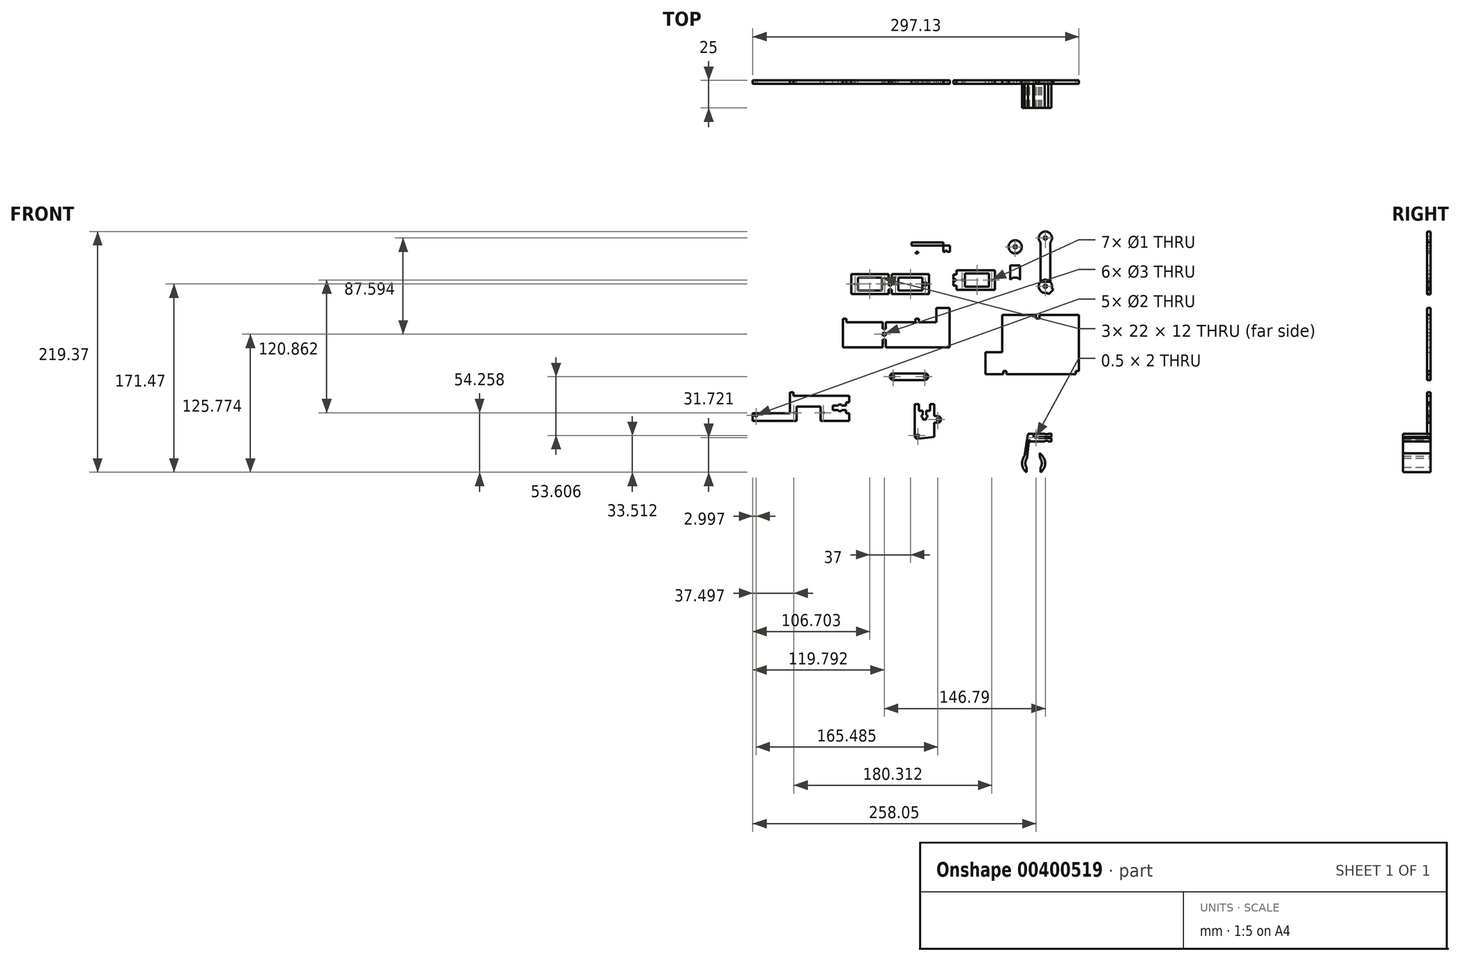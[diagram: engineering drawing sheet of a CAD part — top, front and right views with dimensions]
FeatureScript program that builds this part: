
annotation { "Feature Type Name" : "Feature", "Feature Type Description" : "" }
export const myFeature = defineFeature(function(context is Context, id is Id, definition is map)
    precondition{}
    {
        {
            var Q0;
            Q0=qCreatedBy(makeId("Front.planeOp"),FACE);
            var sketch = newSketch(context, id + "F0", { "sketchPlane" : qUnion([Q0])});
            skLineSegment(sketch, "E0", {"start": v(0, 0) * mm, "end": v(31, 0) * mm});
            skLineSegment(sketch, "E1", {"start": v(31, 0) * mm, "end": v(31, -3) * mm});
            skLineSegment(sketch, "E2", {"start": v(31, -3) * mm, "end": v(34, -3) * mm});
            skLineSegment(sketch, "E3", {"start": v(34, -3) * mm, "end": v(34, 0) * mm});
            skLineSegment(sketch, "E4", {"start": v(34, 0) * mm, "end": v(70, 0) * mm});
            skLineSegment(sketch, "E5", {"start": v(70, 0) * mm, "end": v(70, -51) * mm});
            skLineSegment(sketch, "E6", {"start": v(70, -51) * mm, "end": v(67, -51) * mm});
            skLineSegment(sketch, "E7", {"start": v(67, -51) * mm, "end": v(67, -54) * mm});
            skLineSegment(sketch, "E8", {"start": v(67, -54) * mm, "end": v(4, -54) * mm});
            skLineSegment(sketch, "E9", {"start": v(4, -54) * mm, "end": v(4, -51) * mm});
            skLineSegment(sketch, "E10", {"start": v(4, -51) * mm, "end": v(1, -51) * mm});
            skLineSegment(sketch, "E11", {"start": v(1, -51) * mm, "end": v(1, -54) * mm});
            skLineSegment(sketch, "E12", {"start": v(1, -54) * mm, "end": v(-15, -54) * mm});
            skLineSegment(sketch, "E13", {"start": v(-15, -54) * mm, "end": v(-15, -34) * mm});
            skLineSegment(sketch, "E14", {"start": v(-15, -34) * mm, "end": v(0, -34) * mm});
            skLineSegment(sketch, "E15", {"start": v(0, -34) * mm, "end": v(0, 0) * mm});
            skSolve(sketch);
        }
        {
            var Q0;
            Q0=makeQuery(id+"F0.imprint","IMPRINT",FACE,{"disambiguationData":[TD([[makeQuery(id+"F0.imprint","IMPRINT",EDGE,{"derivedFrom":sQuery(id+"F0.wireOp",EDGE,"E0")}),-1.0]])]});
            extrude(context, id + "F1", {"entities" : qUnion([Q0]), "depth" : 3 * mm});
        }
        {
            var Q0;
            Q0=qCreatedBy(makeId("Front.planeOp"),FACE);
            var sketch = newSketch(context, id + "F2", { "sketchPlane" : qUnion([Q0])});
            skLineSegment(sketch, "E16", {"start": v(-47.84, -29.56) * mm, "end": v(-105.84, -29.56) * mm});
            skLineSegment(sketch, "E17", {"start": v(-105.84, -29.56) * mm, "end": v(-105.84, -22.56) * mm});
            skLineSegment(sketch, "E18", {"start": v(-105.84, -22.56) * mm, "end": v(-108.84, -22.56) * mm});
            skLineSegment(sketch, "E19", {"start": v(-108.84, -22.56) * mm, "end": v(-108.84, -29.56) * mm});
            skPoint(sketch, "E20.endSnap0", {"position": v(-157.78, -10) * mm});
            skLineSegment(sketch, "E21", {"start": v(-108.84, -6.56) * mm, "end": v(-108.84, -12.56) * mm});
            skLineSegment(sketch, "E22", {"start": v(-108.84, -12.56) * mm, "end": v(-105.84, -12.56) * mm});
            skLineSegment(sketch, "E23", {"start": v(-105.84, -12.56) * mm, "end": v(-105.84, -6.56) * mm});
            skLineSegment(sketch, "E24", {"start": v(-105.84, -6.56) * mm, "end": v(-78.84, -6.56) * mm});
            skLineSegment(sketch, "E25", {"start": v(-78.84, -6.56) * mm, "end": v(-78.84, -3.56) * mm});
            skLineSegment(sketch, "E26", {"start": v(-78.84, -3.56) * mm, "end": v(-75.84, -3.56) * mm});
            skLineSegment(sketch, "E27", {"start": v(-75.84, -3.56) * mm, "end": v(-75.84, -6.56) * mm});
            skLineSegment(sketch, "E28", {"start": v(-75.84, -6.56) * mm, "end": v(-59.84, -6.56) * mm});
            skLineSegment(sketch, "E29", {"start": v(-59.84, -6.56) * mm, "end": v(-59.84, 6.44) * mm});
            skLineSegment(sketch, "E30", {"start": v(-59.84, 6.44) * mm, "end": v(-47.84, 6.44) * mm});
            skLineSegment(sketch, "E31", {"start": v(-108.84, -12.56) * mm, "end": v(-107.34, -12.56) * mm});
            skLineSegment(sketch, "E32", {"start": v(-59.84, 6.44) * mm, "end": v(-59.84, 4.44) * mm});
            skLineSegment(sketch, "E33", {"start": v(-58.78, 6.44) * mm, "end": v(-61.78, 6.44) * mm});
            skLineSegment(sketch, "E34.bottom", {"start": v(-62.78, 11) * mm, "end": v(-67.78, 11) * mm});
            skLineSegment(sketch, "E34.top", {"start": v(-62.78, 8) * mm, "end": v(-67.78, 8) * mm});
            skLineSegment(sketch, "E34.left", {"start": v(-62.78, 11) * mm, "end": v(-62.78, 8) * mm});
            skLineSegment(sketch, "E34.right", {"start": v(-67.78, 11) * mm, "end": v(-67.78, 8) * mm});
            skLineSegment(sketch, "E35", {"start": v(-47.84, 6.44) * mm, "end": v(-47.84, -29.56) * mm});
            skLineSegment(sketch, "E36", {"start": v(-108.84, -6.56) * mm, "end": v(-141.84, -6.56) * mm});
            skLineSegment(sketch, "E37", {"start": v(-141.84, -6.56) * mm, "end": v(-141.84, -3.56) * mm});
            skLineSegment(sketch, "E38", {"start": v(-141.84, -3.56) * mm, "end": v(-144.84, -3.56) * mm});
            skLineSegment(sketch, "E39", {"start": v(-144.84, -3.56) * mm, "end": v(-144.84, -6.56) * mm});
            skLineSegment(sketch, "E40", {"start": v(-144.84, -6.56) * mm, "end": v(-144.84, -29.56) * mm});
            skLineSegment(sketch, "E41", {"start": v(-144.84, -29.56) * mm, "end": v(-108.84, -29.56) * mm});
            skLineSegment(sketch, "E42", {"start": v(-108.84, -12.56) * mm, "end": v(-108.84, -17.56) * mm});
            skLineSegment(sketch, "E43", {"start": v(-108.84, -17.56) * mm, "end": v(-107.34, -17.56) * mm});
            skCircle(sketch, "E44", {"center": v(-107.34, -17.56) * mm, "radius": 1.5 * mm});
            skSolve(sketch);
        }
        {
            var Q0;
            Q0=makeQuery(id+"F2.imprint","IMPRINT",FACE,{"disambiguationData":[TD([[makeQuery(id+"F2.imprint","IMPRINT",EDGE,{"derivedFrom":sQuery(id+"F2.wireOp",EDGE,"E16")}),-1.0]])]});
            extrude(context, id + "F3", {"entities" : qUnion([Q0]), "depth" : 3 * mm});
        }
        {
            var Q0;
            Q0=qCreatedBy(makeId("Front.planeOp"),FACE);
            var sketch = newSketch(context, id + "F4", { "sketchPlane" : qUnion([Q0])});
            skLineSegment(sketch, "E45", {"start": v(-66.43, 19.14) * mm, "end": v(-66.43, 37.14) * mm});
            skLineSegment(sketch, "E46", {"start": v(-66.43, 37.14) * mm, "end": v(-100.43, 37.14) * mm});
            skLineSegment(sketch, "E47", {"start": v(-66.43, 19.14) * mm, "end": v(-100.43, 19.14) * mm});
            skLineSegment(sketch, "E48", {"start": v(-100.43, 19.14) * mm, "end": v(-100.43, 23.14) * mm});
            skLineSegment(sketch, "E49", {"start": v(-100.43, 23.14) * mm, "end": v(-103.43, 23.14) * mm});
            skLineSegment(sketch, "E50", {"start": v(-103.43, 23.14) * mm, "end": v(-103.43, 19.14) * mm});
            skLineSegment(sketch, "E51", {"start": v(-100.43, 37.14) * mm, "end": v(-100.43, 33.14) * mm});
            skLineSegment(sketch, "E52", {"start": v(-100.43, 33.14) * mm, "end": v(-103.43, 33.14) * mm});
            skLineSegment(sketch, "E53", {"start": v(-103.43, 33.14) * mm, "end": v(-103.43, 37.14) * mm});
            skLineSegment(sketch, "E54", {"start": v(-103.43, 37.14) * mm, "end": v(-137.43, 37.14) * mm});
            skLineSegment(sketch, "E55", {"start": v(-137.43, 37.14) * mm, "end": v(-137.43, 19.14) * mm});
            skLineSegment(sketch, "E56", {"start": v(-137.43, 19.14) * mm, "end": v(-103.43, 19.14) * mm});
            skLineSegment(sketch, "E57", {"start": v(-137.43, 37.14) * mm, "end": v(-131.43, 37.14) * mm});
            skLineSegment(sketch, "E58.bottom", {"start": v(-131.43, 22.14) * mm, "end": v(-109.43, 22.14) * mm});
            skLineSegment(sketch, "E58.top", {"start": v(-131.43, 34.14) * mm, "end": v(-109.43, 34.14) * mm});
            skLineSegment(sketch, "E58.left", {"start": v(-131.43, 22.14) * mm, "end": v(-131.43, 34.14) * mm});
            skLineSegment(sketch, "E58.right", {"start": v(-109.43, 22.14) * mm, "end": v(-109.43, 34.14) * mm});
            skLineSegment(sketch, "E59", {"start": v(-66.43, 37.14) * mm, "end": v(-72.43, 37.14) * mm});
            skLineSegment(sketch, "E60.bottom", {"start": v(-72.43, 34.14) * mm, "end": v(-94.43, 34.14) * mm});
            skLineSegment(sketch, "E60.top", {"start": v(-72.43, 22.14) * mm, "end": v(-94.43, 22.14) * mm});
            skLineSegment(sketch, "E60.left", {"start": v(-72.43, 34.14) * mm, "end": v(-72.43, 22.14) * mm});
            skLineSegment(sketch, "E60.right", {"start": v(-94.43, 34.14) * mm, "end": v(-94.43, 22.14) * mm});
            skCircle(sketch, "E61", {"center": v(-101.93, 28.14) * mm, "radius": 1.5 * mm});
            skLineSegment(sketch, "E62", {"start": v(-66.43, 37.14) * mm, "end": v(-69.93, 37.14) * mm});
            skCircle(sketch, "E63", {"center": v(-69.93, 28.14) * mm, "radius": 1.5 * mm});
            skLineSegment(sketch, "E64", {"start": v(-131.43, 37.14) * mm, "end": v(-133.93, 37.14) * mm});
            skCircle(sketch, "E65", {"center": v(-133.93, 28.14) * mm, "radius": 0.5 * mm});
            skCircle(sketch, "E66", {"center": v(-106.93, 28.14) * mm, "radius": 0.5 * mm});
            skCircle(sketch, "E67", {"center": v(-96.93, 28.14) * mm, "radius": 0.5 * mm});
            skSolve(sketch);
        }
        {
            var Q0;
            Q0=makeQuery(id+"F4.imprint","IMPRINT",FACE,{"disambiguationData":[TD([[makeQuery(id+"F4.imprint","IMPRINT",EDGE,{"derivedFrom":sQuery(id+"F4.wireOp",EDGE,"E45")}),1.0]])]});
            extrude(context, id + "F5", {"entities" : qUnion([Q0]), "depth" : 3 * mm});
        }
        {
            var Q0;
            Q0=qCreatedBy(makeId("Front.planeOp"),FACE);
            var sketch = newSketch(context, id + "F6", { "sketchPlane" : qUnion([Q0])});
            skLineSegment(sketch, "E68", {"start": v(-6.38, 22.79) * mm, "end": v(-41.38, 22.79) * mm});
            skLineSegment(sketch, "E69", {"start": v(-6.38, 22.79) * mm, "end": v(-6.38, 40.79) * mm});
            skLineSegment(sketch, "E70", {"start": v(-6.38, 40.79) * mm, "end": v(-41.38, 40.79) * mm});
            skLineSegment(sketch, "E71", {"start": v(-41.38, 40.79) * mm, "end": v(-41.38, 36.79) * mm});
            skLineSegment(sketch, "E72", {"start": v(-41.38, 36.79) * mm, "end": v(-44.38, 36.79) * mm});
            skLineSegment(sketch, "E73", {"start": v(-44.38, 36.79) * mm, "end": v(-44.38, 26.79) * mm});
            skLineSegment(sketch, "E74", {"start": v(-44.38, 26.79) * mm, "end": v(-41.38, 26.79) * mm});
            skLineSegment(sketch, "E75", {"start": v(-41.38, 26.79) * mm, "end": v(-41.38, 22.79) * mm});
            skLineSegment(sketch, "E76", {"start": v(-6.38, 40.79) * mm, "end": v(-12.38, 40.79) * mm});
            skLineSegment(sketch, "E77.bottom", {"start": v(-11.82, 37.79) * mm, "end": v(-33.82, 37.79) * mm});
            skLineSegment(sketch, "E77.top", {"start": v(-11.82, 25.79) * mm, "end": v(-33.82, 25.79) * mm});
            skLineSegment(sketch, "E77.left", {"start": v(-11.82, 37.79) * mm, "end": v(-11.82, 25.79) * mm});
            skLineSegment(sketch, "E77.right", {"start": v(-33.82, 37.79) * mm, "end": v(-33.82, 25.79) * mm});
            skLineSegment(sketch, "E78", {"start": v(-12.38, 40.79) * mm, "end": v(-7.38, 40.79) * mm});
            skLineSegment(sketch, "E79", {"start": v(-12.38, 40.79) * mm, "end": v(-9.38, 40.79) * mm});
            skLineSegment(sketch, "E80", {"start": v(-12.38, 40.79) * mm, "end": v(-9.88, 40.79) * mm});
            skLineSegment(sketch, "E81", {"start": v(-33.82, 40.79) * mm, "end": v(-36.32, 40.79) * mm});
            skLineSegment(sketch, "E82", {"start": v(-44.38, 36.79) * mm, "end": v(-44.38, 32.25) * mm});
            skLineSegment(sketch, "E83", {"start": v(-41.38, 36.79) * mm, "end": v(-41.38, 31.79) * mm});
            skLineSegment(sketch, "E84", {"start": v(-41.38, 31.79) * mm, "end": v(-6.38, 31.79) * mm});
            skLineSegment(sketch, "E85", {"start": v(-33.82, 31.79) * mm, "end": v(-34.96, 31.79) * mm});
            skSolve(sketch);
        }
        {
            var Q0;
            {var subQ12=sQuery(id+"F6.wireOp",EDGE,"E71");Q0=makeQuery(id+"F6.imprint","IMPRINT",FACE,{"disambiguationData":[TD([[makeQuery(id+"F6.imprint","IMPRINT",EDGE,{"derivedFrom":subQ12}),1.0]])]});}
            var Q1;
            {var subQ6=sQuery(id+"F6.wireOp",EDGE,"E68");Q1=makeQuery(id+"F6.imprint","IMPRINT",FACE,{"disambiguationData":[TD([[makeQuery(id+"F6.imprint","IMPRINT",EDGE,{"derivedFrom":subQ6}),-1.0]])]});}
            extrude(context, id + "F7", {"entities" : qUnion([Q0, Q1]), "depth" : 3 * mm});
        }
        {
            var Q0;
            Q0=makeQuery(id+"F7.opExtrude","CAP_FACE",FACE,{"disambiguationData":[OSD([sQuery(id+"F6.wireOp",EDGE,"E68"),sQuery(id+"F6.wireOp",EDGE,"E69"),sQuery(id+"F6.wireOp",EDGE,"E70"),sQuery(id+"F6.wireOp",EDGE,"E71"),sQuery(id+"F6.wireOp",EDGE,"E72"),sQuery(id+"F6.wireOp",EDGE,"E73"),sQuery(id+"F6.wireOp",EDGE,"E74"),sQuery(id+"F6.wireOp",EDGE,"E75"),sQuery(id+"F6.wireOp",EDGE,"E76"),sQuery(id+"F6.wireOp",EDGE,"E77.bottom"),sQuery(id+"F6.wireOp",EDGE,"E77.top"),sQuery(id+"F6.wireOp",EDGE,"E77.left"),sQuery(id+"F6.wireOp",EDGE,"E77.right"),sQuery(id+"F6.wireOp",EDGE,"E78"),sQuery(id+"F6.wireOp",EDGE,"E79"),sQuery(id+"F6.wireOp",EDGE,"E80"),sQuery(id+"F6.wireOp",EDGE,"E81"),sQuery(id+"F6.wireOp",EDGE,"E82")])],"isStart":false});
            var sketch = newSketch(context, id + "F8", { "sketchPlane" : qUnion([Q0])});
            skCircle(sketch, "E86", {"center": v(-36.32, 31.79) * mm, "radius": 0.5 * mm});
            skLineSegment(sketch, "E87", {"start": v(-9.32, 31.79) * mm, "end": v(-9.7, 31.79) * mm});
            skCircle(sketch, "E88", {"center": v(-9.32, 31.79) * mm, "radius": 0.5 * mm});
            skLineSegment(sketch, "E89", {"start": v(-44.38, 36.79) * mm, "end": v(-44.38, 31.79) * mm});
            skLineSegment(sketch, "E90", {"start": v(-44.38, 31.79) * mm, "end": v(-43.38, 31.79) * mm});
            skCircle(sketch, "E91", {"center": v(-43.38, 31.79) * mm, "radius": 1 * mm});
            skSolve(sketch);
        }
        {
            var Q0;
            Q0=makeQuery(id+"F8.imprint","IMPRINT",FACE,{"disambiguationData":[TD([[makeQuery(id+"F8.imprint","IMPRINT",EDGE,{"derivedFrom":sQuery(id+"F8.wireOp",EDGE,"E86")}),1.0]])]});
            var Q1;
            Q1=makeQuery(id+"F8.imprint","IMPRINT",FACE,{"disambiguationData":[TD([[makeQuery(id+"F8.imprint","IMPRINT",EDGE,{"derivedFrom":sQuery(id+"F8.wireOp",EDGE,"E88")}),1.0]])]});
            extrude(context, id + "F9", {"entities" : qUnion([Q0, Q1]), "operationType" : NewBodyOperationType.REMOVE, "oppositeDirection" : true, "depth" : 25 * mm});
        }
        {
            var Q0;
            Q0=makeQuery(id+"F8.imprint","IMPRINT",FACE,{"disambiguationData":[TD([[makeQuery(id+"F8.imprint","IMPRINT",EDGE,{"derivedFrom":sQuery(id+"F8.wireOp",EDGE,"E86")}),-1.0]])]});
            var sketch = newSketch(context, id + "F10", { "sketchPlane" : qUnion([Q0])});
            skCircle(sketch, "E92", {"center": v(-43.41, 31.78) * mm, "radius": 1 * mm});
            skSolve(sketch);
        }
        {
            var Q0;
            Q0 = qSketchRegion(id + "F10", true);
            extrude(context, id + "F11", {"entities" : qUnion([Q0]), "operationType" : NewBodyOperationType.REMOVE, "oppositeDirection" : true, "depth" : 25 * mm});
        }
        {
            var Q0;
            Q0=qCreatedBy(makeId("Front.planeOp"),FACE);
            var sketch = newSketch(context, id + "F12", { "sketchPlane" : qUnion([Q0])});
            skLineSegment(sketch, "E93", {"start": v(-227.13, -96.57) * mm, "end": v(-187.13, -96.57) * mm});
            skLineSegment(sketch, "E94", {"start": v(-187.13, -96.57) * mm, "end": v(-187.13, -83.57) * mm});
            skLineSegment(sketch, "E95", {"start": v(-187.13, -83.57) * mm, "end": v(-165.13, -83.57) * mm});
            skLineSegment(sketch, "E96", {"start": v(-165.13, -83.57) * mm, "end": v(-165.13, -96.57) * mm});
            skLineSegment(sketch, "E97", {"start": v(-165.13, -96.57) * mm, "end": v(-139.13, -96.57) * mm});
            skLineSegment(sketch, "E98", {"start": v(-227.13, -96.57) * mm, "end": v(-227.13, -89.57) * mm});
            skLineSegment(sketch, "E99", {"start": v(-227.13, -89.57) * mm, "end": v(-193.13, -89.57) * mm});
            skLineSegment(sketch, "E100", {"start": v(-193.13, -89.57) * mm, "end": v(-193.13, -70.57) * mm});
            skLineSegment(sketch, "E101", {"start": v(-193.13, -70.57) * mm, "end": v(-190.13, -70.57) * mm});
            skLineSegment(sketch, "E102", {"start": v(-139.13, -96.57) * mm, "end": v(-139.13, -89.57) * mm});
            skLineSegment(sketch, "E103", {"start": v(-139.13, -89.57) * mm, "end": v(-142.13, -89.57) * mm});
            skLineSegment(sketch, "E104", {"start": v(-190.13, -70.57) * mm, "end": v(-190.13, -73.57) * mm});
            skLineSegment(sketch, "E105", {"start": v(-190.13, -73.57) * mm, "end": v(-139.13, -73.57) * mm});
            skLineSegment(sketch, "E106", {"start": v(-139.13, -73.57) * mm, "end": v(-139.13, -79.57) * mm});
            skLineSegment(sketch, "E107", {"start": v(-139.13, -79.57) * mm, "end": v(-142.13, -79.57) * mm});
            skLineSegment(sketch, "E108", {"start": v(-142.13, -79.57) * mm, "end": v(-142.13, -82.57) * mm});
            skLineSegment(sketch, "E109", {"start": v(-142.13, -82.57) * mm, "end": v(-146.13, -82.57) * mm});
            skLineSegment(sketch, "E110", {"start": v(-142.13, -89.57) * mm, "end": v(-142.13, -86.57) * mm});
            skLineSegment(sketch, "E111", {"start": v(-142.13, -86.57) * mm, "end": v(-146.13, -86.57) * mm});
            skLineSegment(sketch, "E112", {"start": v(-146.13, -82.57) * mm, "end": v(-146.13, -81.57) * mm});
            skLineSegment(sketch, "E113", {"start": v(-146.13, -81.57) * mm, "end": v(-149.13, -81.57) * mm});
            skLineSegment(sketch, "E114", {"start": v(-149.13, -81.57) * mm, "end": v(-149.13, -82.57) * mm});
            skLineSegment(sketch, "E115", {"start": v(-149.13, -82.57) * mm, "end": v(-154.13, -82.57) * mm});
            skLineSegment(sketch, "E116", {"start": v(-154.13, -82.57) * mm, "end": v(-154.13, -86.57) * mm});
            skLineSegment(sketch, "E117", {"start": v(-154.13, -86.57) * mm, "end": v(-149.13, -86.57) * mm});
            skLineSegment(sketch, "E118", {"start": v(-149.13, -86.57) * mm, "end": v(-149.13, -87.57) * mm});
            skLineSegment(sketch, "E119", {"start": v(-149.13, -87.57) * mm, "end": v(-146.13, -87.57) * mm});
            skLineSegment(sketch, "E120", {"start": v(-146.13, -87.57) * mm, "end": v(-146.13, -86.57) * mm});
            skSolve(sketch);
        }
        {
            var Q0;
            Q0=makeQuery(id+"F12.imprint","IMPRINT",FACE,{"disambiguationData":[TD([[makeQuery(id+"F12.imprint","IMPRINT",EDGE,{"derivedFrom":sQuery(id+"F12.wireOp",EDGE,"E93")}),1.0]])]});
            extrude(context, id + "F13", {"entities" : qUnion([Q0]), "depth" : 3 * mm});
        }
        {
            var Q0;
            Q0=makeQuery(id+"F13.opExtrude","CAP_FACE",FACE,{"disambiguationData":[OSD([sQuery(id+"F12.wireOp",EDGE,"E93"),sQuery(id+"F12.wireOp",EDGE,"E94"),sQuery(id+"F12.wireOp",EDGE,"E95"),sQuery(id+"F12.wireOp",EDGE,"E96"),sQuery(id+"F12.wireOp",EDGE,"E97"),sQuery(id+"F12.wireOp",EDGE,"E98"),sQuery(id+"F12.wireOp",EDGE,"E99"),sQuery(id+"F12.wireOp",EDGE,"E100"),sQuery(id+"F12.wireOp",EDGE,"E101"),sQuery(id+"F12.wireOp",EDGE,"E102"),sQuery(id+"F12.wireOp",EDGE,"E103"),sQuery(id+"F12.wireOp",EDGE,"E104"),sQuery(id+"F12.wireOp",EDGE,"E105"),sQuery(id+"F12.wireOp",EDGE,"E106"),sQuery(id+"F12.wireOp",EDGE,"E107"),sQuery(id+"F12.wireOp",EDGE,"E108"),sQuery(id+"F12.wireOp",EDGE,"E109"),sQuery(id+"F12.wireOp",EDGE,"E110"),sQuery(id+"F12.wireOp",EDGE,"E111"),sQuery(id+"F12.wireOp",EDGE,"E112"),sQuery(id+"F12.wireOp",EDGE,"E113"),sQuery(id+"F12.wireOp",EDGE,"E114"),sQuery(id+"F12.wireOp",EDGE,"E115"),sQuery(id+"F12.wireOp",EDGE,"E116"),sQuery(id+"F12.wireOp",EDGE,"E117"),sQuery(id+"F12.wireOp",EDGE,"E118"),sQuery(id+"F12.wireOp",EDGE,"E119"),sQuery(id+"F12.wireOp",EDGE,"E120")])],"isStart":false});
            var sketch = newSketch(context, id + "F14", { "sketchPlane" : qUnion([Q0])});
            skCircle(sketch, "E121", {"center": v(-224.13, -91.57) * mm, "radius": 1 * mm});
            skCircle(sketch, "E122", {"center": v(-189.63, -89.07) * mm, "radius": 0.5 * mm});
            skCircle(sketch, "E123", {"center": v(-162.63, -89.07) * mm, "radius": 0.5 * mm});
            skSolve(sketch);
        }
        {
            var Q0;
            Q0=makeQuery(id+"F14.imprint","IMPRINT",FACE,{"disambiguationData":[TD([[makeQuery(id+"F14.imprint","IMPRINT",EDGE,{"derivedFrom":sQuery(id+"F14.wireOp",EDGE,"E121")}),1.0]])]});
            var Q1;
            Q1=makeQuery(id+"F14.imprint","IMPRINT",FACE,{"disambiguationData":[TD([[makeQuery(id+"F14.imprint","IMPRINT",EDGE,{"derivedFrom":sQuery(id+"F14.wireOp",EDGE,"E122")}),1.0]])]});
            var Q2;
            Q2=makeQuery(id+"F14.imprint","IMPRINT",FACE,{"disambiguationData":[TD([[makeQuery(id+"F14.imprint","IMPRINT",EDGE,{"derivedFrom":sQuery(id+"F14.wireOp",EDGE,"E123")}),1.0]])]});
            extrude(context, id + "F15", {"entities" : qUnion([Q0, Q1, Q2]), "operationType" : NewBodyOperationType.REMOVE, "oppositeDirection" : true, "depth" : 25 * mm});
        }
        {
            var Q0;
            Q0=qCreatedBy(makeId("Front.planeOp"),FACE);
            var sketch = newSketch(context, id + "F16", { "sketchPlane" : qUnion([Q0])});
            skLineSegment(sketch, "E124.bottom", {"start": v(-99.2, -53.21) * mm, "end": v(-70.2, -53.21) * mm});
            skLineSegment(sketch, "E124.top", {"start": v(-99.2, -59.21) * mm, "end": v(-70.2, -59.21) * mm});
            skLineSegment(sketch, "E124.left", {"start": v(-102.2, -56.21) * mm, "end": v(-102.2, -56.21) * mm});
            skLineSegment(sketch, "E124.right", {"start": v(-67.2, -56.21) * mm, "end": v(-67.2, -56.21) * mm});
            skPoint(sketch, "E125.visualSharp", {"position": v(-102.2, -53.21) * mm});
            skArc(sketch, "E125.filletArc", {"start": v(-99.2, -53.21) * mm, "mid": v(-101.33, -54.1) * mm, "end": v(-102.2, -56.21) * mm});
            skPoint(sketch, "E126.visualSharp", {"position": v(-102.2, -59.21) * mm});
            skArc(sketch, "E126.filletArc", {"start": v(-102.2, -56.21) * mm, "mid": v(-101.33, -58.33) * mm, "end": v(-99.2, -59.21) * mm});
            skPoint(sketch, "E127.visualSharp", {"position": v(-67.2, -53.21) * mm});
            skArc(sketch, "E127.filletArc", {"start": v(-67.2, -56.21) * mm, "mid": v(-68.09, -54.1) * mm, "end": v(-70.2, -53.21) * mm});
            skPoint(sketch, "E128.visualSharp", {"position": v(-67.2, -59.21) * mm});
            skArc(sketch, "E128.filletArc", {"start": v(-70.2, -59.21) * mm, "mid": v(-68.09, -58.33) * mm, "end": v(-67.2, -56.21) * mm});
            skLineSegment(sketch, "E129", {"start": v(-102.2, -56.21) * mm, "end": v(-66.67, -56.21) * mm});
            skLineSegment(sketch, "E130", {"start": v(-102.2, -56.21) * mm, "end": v(-99.2, -56.21) * mm});
            skLineSegment(sketch, "E131", {"start": v(-99.2, -56.21) * mm, "end": v(-70.2, -56.21) * mm});
            skCircle(sketch, "E132", {"center": v(-99.2, -56.21) * mm, "radius": 1 * mm});
            skCircle(sketch, "E133", {"center": v(-70.2, -56.21) * mm, "radius": 1 * mm});
            skSolve(sketch);
        }
        {
            var Q0;
            Q0=makeQuery(id+"F16.imprint","IMPRINT",FACE,{"disambiguationData":[TD([[makeQuery(id+"F16.imprint","IMPRINT",EDGE,{"derivedFrom":sQuery(id+"F16.wireOp",EDGE,"E124.top")}),1.0]])]});
            var Q1;
            Q1=makeQuery(id+"F16.imprint","IMPRINT",FACE,{"disambiguationData":[TD([[makeQuery(id+"F16.imprint","IMPRINT",EDGE,{"derivedFrom":sQuery(id+"F16.wireOp",EDGE,"E124.bottom")}),-1.0]])]});
            extrude(context, id + "F17", {"entities" : qUnion([Q0, Q1]), "depth" : 3 * mm});
        }
        {
            var Q0;
            Q0=qCreatedBy(makeId("Front.planeOp"),FACE);
            var sketch = newSketch(context, id + "F18", { "sketchPlane" : qUnion([Q0])});
            skLineSegment(sketch, "E134", {"start": v(-75.65, -87.17) * mm, "end": v(-72.15, -87.17) * mm});
            skLineSegment(sketch, "E135", {"start": v(-72.15, -87.17) * mm, "end": v(-72.15, -91.17) * mm});
            skLineSegment(sketch, "E136", {"start": v(-72.15, -91.17) * mm, "end": v(-73.15, -91.17) * mm});
            skLineSegment(sketch, "E137", {"start": v(-73.15, -91.17) * mm, "end": v(-73.15, -93.17) * mm});
            skLineSegment(sketch, "E138", {"start": v(-73.15, -93.17) * mm, "end": v(-72.15, -93.17) * mm});
            skLineSegment(sketch, "E139", {"start": v(-72.15, -93.17) * mm, "end": v(-72.15, -95.17) * mm});
            skLineSegment(sketch, "E140", {"start": v(-72.15, -95.17) * mm, "end": v(-69.15, -95.17) * mm});
            skLineSegment(sketch, "E141", {"start": v(-69.15, -95.17) * mm, "end": v(-69.15, -93.17) * mm});
            skLineSegment(sketch, "E142", {"start": v(-69.15, -93.17) * mm, "end": v(-68.15, -93.17) * mm});
            skLineSegment(sketch, "E143", {"start": v(-68.15, -93.17) * mm, "end": v(-68.15, -91.17) * mm});
            skLineSegment(sketch, "E144", {"start": v(-68.15, -91.17) * mm, "end": v(-69.15, -91.17) * mm});
            skLineSegment(sketch, "E145", {"start": v(-69.15, -91.17) * mm, "end": v(-69.15, -87.17) * mm});
            skLineSegment(sketch, "E146", {"start": v(-65.65, -87.17) * mm, "end": v(-65.65, -81.17) * mm});
            skLineSegment(sketch, "E147", {"start": v(-65.65, -81.17) * mm, "end": v(-61.65, -81.17) * mm});
            skLineSegment(sketch, "E148", {"start": v(-61.65, -81.17) * mm, "end": v(-61.65, -92.17) * mm});
            skLineSegment(sketch, "E149", {"start": v(-61.65, -92.17) * mm, "end": v(-58.65, -92.17) * mm});
            skLineSegment(sketch, "E150", {"start": v(-55.65, -95.17) * mm, "end": v(-55.65, -95.17) * mm});
            skLineSegment(sketch, "E151", {"start": v(-58.65, -98.17) * mm, "end": v(-61.65, -98.17) * mm});
            skLineSegment(sketch, "E152", {"start": v(-61.65, -98.17) * mm, "end": v(-61.65, -111.17) * mm});
            skPoint(sketch, "E153.visualSharp", {"position": v(-55.65, -98.17) * mm});
            skArc(sketch, "E153.filletArc", {"start": v(-58.65, -98.17) * mm, "mid": v(-56.53, -97.3) * mm, "end": v(-55.65, -95.17) * mm});
            skPoint(sketch, "E154.visualSharp", {"position": v(-55.65, -92.17) * mm});
            skArc(sketch, "E154.filletArc", {"start": v(-55.65, -95.17) * mm, "mid": v(-56.53, -93.05) * mm, "end": v(-58.65, -92.17) * mm});
            skLineSegment(sketch, "E155", {"start": v(-55.65, -95.17) * mm, "end": v(-57.65, -95.17) * mm});
            skLineSegment(sketch, "E156", {"start": v(-57.65, -95.17) * mm, "end": v(-58.65, -95.17) * mm});
            skCircle(sketch, "E157", {"center": v(-58.65, -95.17) * mm, "radius": 1 * mm});
            skLineSegment(sketch, "E158", {"start": v(-69.15, -87.17) * mm, "end": v(-65.65, -87.17) * mm});
            skLineSegment(sketch, "E159", {"start": v(-75.65, -87.17) * mm, "end": v(-75.65, -81.17) * mm});
            skLineSegment(sketch, "E160", {"start": v(-75.65, -81.17) * mm, "end": v(-79.65, -81.17) * mm});
            skLineSegment(sketch, "E161", {"start": v(-79.65, -81.17) * mm, "end": v(-79.65, -109.82) * mm});
            skLineSegment(sketch, "E162", {"start": v(-76.32, -112.8) * mm, "end": v(-61.65, -111.17) * mm});
            skPoint(sketch, "E163.visualSharp", {"position": v(-79.65, -113.17) * mm});
            skArc(sketch, "E163.filletArc", {"start": v(-79.65, -109.82) * mm, "mid": v(-78.65, -112.05) * mm, "end": v(-76.32, -112.8) * mm});
            skCircle(sketch, "E164", {"center": v(-76.65, -109.82) * mm, "radius": 1 * mm});
            skSolve(sketch);
        }
        {
            var Q0;
            Q0=makeQuery(id+"F18.imprint","IMPRINT",FACE,{"disambiguationData":[TD([[makeQuery(id+"F18.imprint","IMPRINT",EDGE,{"derivedFrom":sQuery(id+"F18.wireOp",EDGE,"E134")}),-1.0]])]});
            extrude(context, id + "F19", {"entities" : qUnion([Q0]), "depth" : 3 * mm});
        }
        {
            var Q0;
            Q0=qCreatedBy(makeId("Front.planeOp"),FACE);
            var sketch = newSketch(context, id + "F20", { "sketchPlane" : qUnion([Q0])});
            skLineSegment(sketch, "E165", {"start": v(11.96, 45.07) * mm, "end": v(16.46, 45.07) * mm});
            skLineSegment(sketch, "E166", {"start": v(16.46, 45.07) * mm, "end": v(7.46, 45.07) * mm});
            skLineSegment(sketch, "E167", {"start": v(16.46, 45.07) * mm, "end": v(16.46, 58.57) * mm});
            skLineSegment(sketch, "E168", {"start": v(16.46, 58.57) * mm, "end": v(16.46, 31.57) * mm});
            skLineSegment(sketch, "E169", {"start": v(7.46, 45.07) * mm, "end": v(7.46, 58.57) * mm});
            skLineSegment(sketch, "E170", {"start": v(7.46, 58.57) * mm, "end": v(7.46, 31.57) * mm});
            skLineSegment(sketch, "E171", {"start": v(11.96, 45.07) * mm, "end": v(11.96, 22.07) * mm});
            skLineSegment(sketch, "E172", {"start": v(11.96, 22.07) * mm, "end": v(11.96, 45.07) * mm});
            skLineSegment(sketch, "E173", {"start": v(11.96, 45.07) * mm, "end": v(11.96, 68.07) * mm});
            skLineSegment(sketch, "E174", {"start": v(11.96, 22.07) * mm, "end": v(11.96, 28.07) * mm});
            skCircle(sketch, "E175", {"center": v(11.96, 28.07) * mm, "radius": 6 * mm});
            skLineSegment(sketch, "E176", {"start": v(11.96, 68.07) * mm, "end": v(11.96, 62.07) * mm});
            skCircle(sketch, "E177", {"center": v(11.96, 62.07) * mm, "radius": 6 * mm});
            skCircle(sketch, "E178", {"center": v(11.96, 62.07) * mm, "radius": 1.5 * mm});
            skCircle(sketch, "E179", {"center": v(11.96, 28.07) * mm, "radius": 1.5 * mm});
            skSolve(sketch);
        }
        {
            var Q0;
            {var subQ0=sQuery(id+"F20.wireOp",EDGE,"E170");var subQ1=sQuery(id+"F20.wireOp",EDGE,"E166");var subQ2=makeQuery(id+"F20.imprint","INTERSECT",VERTEX,{"derivedFrom":[subQ1,subQ0]});Q0=makeQuery(id+"F20.imprint","IMPRINT",FACE,{"disambiguationData":[TD([[makeQuery(id+"F20.imprint","IMPRINT",EDGE,{"disambiguationData":[TD([[subQ2,-1.0]])],"derivedFrom":subQ0}),1.0]])]});}
            var Q1;
            {var subQ0=sQuery(id+"F20.wireOp",EDGE,"E168");var subQ1=sQuery(id+"F20.wireOp",EDGE,"E166");var subQ2=makeQuery(id+"F20.imprint","INTERSECT",VERTEX,{"derivedFrom":[subQ1,subQ0]});Q1=makeQuery(id+"F20.imprint","IMPRINT",FACE,{"disambiguationData":[TD([[makeQuery(id+"F20.imprint","IMPRINT",EDGE,{"disambiguationData":[TD([[subQ2,-1.0]])],"derivedFrom":subQ0}),-1.0]])]});}
            var Q2;
            {var subQ4=sQuery(id+"F20.wireOp",EDGE,"E172");var subQ6=sQuery(id+"F20.wireOp",EDGE,"E179");var subQ7=makeQuery(id+"F20.imprint","INTERSECT",VERTEX,{"derivedFrom":[subQ4,subQ6]});Q2=makeQuery(id+"F20.imprint","IMPRINT",FACE,{"disambiguationData":[TD([[makeQuery(id+"F20.imprint","IMPRINT",EDGE,{"disambiguationData":[TD([[subQ7,-1.0]])],"derivedFrom":subQ4}),1.0]])]});}
            var Q3;
            {var subQ2=sQuery(id+"F20.wireOp",EDGE,"E172");var subQ6=sQuery(id+"F20.wireOp",EDGE,"E179");var subQ8=makeQuery(id+"F20.imprint","INTERSECT",VERTEX,{"derivedFrom":[subQ2,subQ6]});Q3=makeQuery(id+"F20.imprint","IMPRINT",FACE,{"disambiguationData":[TD([[makeQuery(id+"F20.imprint","IMPRINT",EDGE,{"disambiguationData":[TD([[subQ8,-1.0]])],"derivedFrom":subQ2}),-1.0]])]});}
            var Q4;
            {var subQ0=sQuery(id+"F20.wireOp",EDGE,"E170");var subQ1=sQuery(id+"F20.wireOp",EDGE,"E166");var subQ2=makeQuery(id+"F20.imprint","INTERSECT",VERTEX,{"derivedFrom":[subQ1,subQ0]});Q4=makeQuery(id+"F20.imprint","IMPRINT",FACE,{"disambiguationData":[TD([[makeQuery(id+"F20.imprint","IMPRINT",EDGE,{"disambiguationData":[TD([[subQ2,1.0]])],"derivedFrom":subQ0}),1.0]])]});}
            var Q5;
            {var subQ0=sQuery(id+"F20.wireOp",EDGE,"E168");var subQ1=sQuery(id+"F20.wireOp",EDGE,"E166");var subQ2=makeQuery(id+"F20.imprint","INTERSECT",VERTEX,{"derivedFrom":[subQ1,subQ0]});Q5=makeQuery(id+"F20.imprint","IMPRINT",FACE,{"disambiguationData":[TD([[makeQuery(id+"F20.imprint","IMPRINT",EDGE,{"disambiguationData":[TD([[subQ2,1.0]])],"derivedFrom":subQ0}),-1.0]])]});}
            var Q6;
            {var subQ0=sQuery(id+"F20.wireOp",EDGE,"E177");var subQ2=sQuery(id+"F20.wireOp",EDGE,"E173");var subQ3=makeQuery(id+"F20.imprint","INTERSECT",VERTEX,{"derivedFrom":[subQ2,subQ0]});Q6=makeQuery(id+"F20.imprint","IMPRINT",FACE,{"disambiguationData":[TD([[makeQuery(id+"F20.imprint","IMPRINT",EDGE,{"disambiguationData":[TD([[subQ3,-1.0]])],"derivedFrom":subQ2}),1.0]])]});}
            var Q7;
            {var subQ0=sQuery(id+"F20.wireOp",EDGE,"E177");var subQ2=sQuery(id+"F20.wireOp",EDGE,"E173");var subQ3=makeQuery(id+"F20.imprint","INTERSECT",VERTEX,{"derivedFrom":[subQ2,subQ0]});Q7=makeQuery(id+"F20.imprint","IMPRINT",FACE,{"disambiguationData":[TD([[makeQuery(id+"F20.imprint","IMPRINT",EDGE,{"disambiguationData":[TD([[subQ3,-1.0]])],"derivedFrom":subQ2}),-1.0]])]});}
            extrude(context, id + "F21", {"entities" : qUnion([Q0, Q1, Q2, Q3, Q4, Q5, Q6, Q7]), "depth" : 3 * mm});
        }
        {
            var Q0;
            Q0=qCreatedBy(makeId("Front.planeOp"),FACE);
            var sketch = newSketch(context, id + "F22", { "sketchPlane" : qUnion([Q0])});
            skLineSegment(sketch, "E180", {"start": v(34.95, 66.04) * mm, "end": v(34.95, 30.04) * mm});
            skLineSegment(sketch, "E181", {"start": v(34.95, 30.04) * mm, "end": v(34.95, 48.04) * mm});
            skLineSegment(sketch, "E182", {"start": v(43.95, 48.04) * mm, "end": v(43.95, 30.04) * mm});
            skLineSegment(sketch, "E183", {"start": v(43.95, 30.04) * mm, "end": v(43.95, 66.04) * mm});
            skLineSegment(sketch, "E184", {"start": v(39.45, 76.04) * mm, "end": v(39.45, 70.04) * mm});
            skLineSegment(sketch, "E185", {"start": v(39.45, 20.04) * mm, "end": v(39.45, 26.04) * mm});
            skCircle(sketch, "E186", {"center": v(39.45, 26.04) * mm, "radius": 6 * mm});
            skCircle(sketch, "E187", {"center": v(39.45, 70.04) * mm, "radius": 6 * mm});
            skCircle(sketch, "E188", {"center": v(39.45, 70.04) * mm, "radius": 1.5 * mm});
            skCircle(sketch, "E189", {"center": v(39.45, 26.04) * mm, "radius": 1.5 * mm});
            skLineSegment(sketch, "E190.bottom", {"start": v(39.45, 26.04) * mm, "end": v(39.45, 26.04) * mm});
            skLineSegment(sketch, "E190.top", {"start": v(39.45, 20.04) * mm, "end": v(39.45, 20.04) * mm});
            skLineSegment(sketch, "E190.left", {"start": v(39.45, 26.04) * mm, "end": v(39.45, 20.04) * mm});
            skLineSegment(sketch, "E190.right", {"start": v(39.45, 26.04) * mm, "end": v(39.45, 20.04) * mm});
            skLineSegment(sketch, "E191.bottom", {"start": v(39.45, 26.04) * mm, "end": v(45.45, 26.04) * mm});
            skLineSegment(sketch, "E192", {"start": v(39.45, 26.04) * mm, "end": v(45.45, 20.04) * mm});
            skLineSegment(sketch, "E193", {"start": v(39.45, 26.04) * mm, "end": v(58.6, 6.9) * mm});
            skLineSegment(sketch, "E194", {"start": v(42.42, 18.83) * mm, "end": v(41, 20.24) * mm});
            skLineSegment(sketch, "E195", {"start": v(46.66, 23.07) * mm, "end": v(45.25, 24.49) * mm});
            skLineSegment(sketch, "E196", {"start": v(42.42, 18.83) * mm, "end": v(46.66, 23.07) * mm});
            skLineSegment(sketch, "E197", {"start": v(39.45, 26.04) * mm, "end": v(45.1, 20.38) * mm});
            skLineSegment(sketch, "E198", {"start": v(45.1, 20.38) * mm, "end": v(47.23, 18.26) * mm});
            skLineSegment(sketch, "E199", {"start": v(45.1, 20.38) * mm, "end": v(47.05, 18.44) * mm});
            skLineSegment(sketch, "E200", {"start": v(40.51, 24.98) * mm, "end": v(46.17, 19.32) * mm});
            skLineSegment(sketch, "E201", {"start": v(46.17, 19.32) * mm, "end": v(48.64, 16.85) * mm});
            skCircle(sketch, "E202", {"center": v(48.64, 16.85) * mm, "radius": 3.5 * mm});
            skCircle(sketch, "E203", {"center": v(48.64, 16.85) * mm, "radius": 7 * mm});
            skLineSegment(sketch, "E204", {"start": v(48.64, 16.85) * mm, "end": v(49.57, 9.9) * mm});
            skLineSegment(sketch, "E205", {"start": v(49.57, 9.9) * mm, "end": v(48.64, 16.85) * mm});
            skLineSegment(sketch, "E206", {"start": v(48.64, 16.85) * mm, "end": v(55.31, 14.72) * mm});
            skLineSegment(sketch, "E207", {"start": v(34.95, 30.04) * mm, "end": v(34.95, 66.04) * mm});
            skLineSegment(sketch, "E208", {"start": v(43.95, 66.04) * mm, "end": v(43.95, 30.04) * mm});
            skLineSegment(sketch, "E209.bottom", {"start": v(34.95, 66.04) * mm, "end": v(43.95, 66.04) * mm});
            skLineSegment(sketch, "E209.top", {"start": v(34.95, 30.04) * mm, "end": v(43.95, 30.04) * mm});
            skSolve(sketch);
        }
        {
            var Q0;
            {var subQ1=sQuery(id+"F22.wireOp",EDGE,"E209.bottom");var subQ3=sQuery(id+"F22.wireOp",EDGE,"E187");var subQ5=makeQuery(id+"F22.imprint","INTERSECT",VERTEX,{"disambiguationData":[OD(0.0)],"derivedFrom":[subQ3,subQ1]});Q0=makeQuery(id+"F22.imprint","IMPRINT",FACE,{"disambiguationData":[TD([[makeQuery(id+"F22.imprint","IMPRINT",EDGE,{"disambiguationData":[TD([[subQ5,-1.0]])],"derivedFrom":subQ3}),-1.0]])]});}
            var Q1;
            Q1=makeQuery(id+"F22.imprint","IMPRINT",FACE,{"disambiguationData":[TD([[makeQuery(id+"F22.imprint","IMPRINT",EDGE,{"derivedFrom":sQuery(id+"F22.wireOp",EDGE,"E188")}),-1.0]])]});
            var Q2;
            {var subQ6=sQuery(id+"F22.wireOp",EDGE,"E190.left");var subQ8=sQuery(id+"F22.wireOp",EDGE,"E189");var subQ9=makeQuery(id+"F22.imprint","INTERSECT",VERTEX,{"derivedFrom":[subQ8,subQ6]});Q2=makeQuery(id+"F22.imprint","IMPRINT",FACE,{"disambiguationData":[TD([[makeQuery(id+"F22.imprint","IMPRINT",EDGE,{"disambiguationData":[TD([[subQ9,1.0]])],"derivedFrom":subQ8}),-1.0]])]});}
            var Q3;
            {var subQ0=sQuery(id+"F22.wireOp",EDGE,"E209.top");var subQ1=sQuery(id+"F22.wireOp",EDGE,"E186");var subQ2=makeQuery(id+"F22.imprint","INTERSECT",VERTEX,{"disambiguationData":[OD(0.0)],"derivedFrom":[subQ1,subQ0]});Q3=makeQuery(id+"F22.imprint","IMPRINT",FACE,{"disambiguationData":[TD([[makeQuery(id+"F22.imprint","IMPRINT",EDGE,{"disambiguationData":[TD([[subQ2,-1.0]])],"derivedFrom":subQ1}),1.0]])]});}
            var Q4;
            {var subQ0=sQuery(id+"F22.wireOp",EDGE,"E209.bottom");var subQ1=sQuery(id+"F22.wireOp",EDGE,"E187");var subQ2=makeQuery(id+"F22.imprint","INTERSECT",VERTEX,{"disambiguationData":[OD(0.0)],"derivedFrom":[subQ1,subQ0]});Q4=makeQuery(id+"F22.imprint","IMPRINT",FACE,{"disambiguationData":[TD([[makeQuery(id+"F22.imprint","IMPRINT",EDGE,{"disambiguationData":[TD([[subQ2,-1.0]])],"derivedFrom":subQ1}),1.0]])]});}
            var Q5;
            {var subQ0=sQuery(id+"F22.wireOp",EDGE,"E186");var subQ6=sQuery(id+"F22.wireOp",EDGE,"E191.bottom");var subQ8=makeQuery(id+"F22.imprint","INTERSECT",VERTEX,{"derivedFrom":[subQ6,subQ0]});Q5=makeQuery(id+"F22.imprint","IMPRINT",FACE,{"disambiguationData":[TD([[makeQuery(id+"F22.imprint","IMPRINT",EDGE,{"disambiguationData":[TD([[subQ8,1.0]])],"derivedFrom":subQ6}),-1.0]])]});}
            var Q6;
            {var subQ0=sQuery(id+"F22.wireOp",EDGE,"E186");var subQ1=sQuery(id+"F22.wireOp",EDGE,"E190.left");var subQ2=makeQuery(id+"F22.imprint","INTERSECT",VERTEX,{"derivedFrom":[subQ1,subQ0]});Q6=makeQuery(id+"F22.imprint","IMPRINT",FACE,{"disambiguationData":[TD([[makeQuery(id+"F22.imprint","IMPRINT",EDGE,{"disambiguationData":[TD([[subQ2,1.0]])],"derivedFrom":subQ1}),1.0]])]});}
            var Q7;
            {var subQ0=sQuery(id+"F22.wireOp",EDGE,"E186");var subQ1=sQuery(id+"F22.wireOp",EDGE,"E194");var subQ2=makeQuery(id+"F22.imprint","INTERSECT",VERTEX,{"derivedFrom":[subQ1,subQ0]});Q7=makeQuery(id+"F22.imprint","IMPRINT",FACE,{"disambiguationData":[TD([[makeQuery(id+"F22.imprint","IMPRINT",EDGE,{"disambiguationData":[TD([[subQ2,1.0]])],"derivedFrom":subQ1}),-1.0]])]});}
            var Q8;
            {var subQ0=sQuery(id+"F22.wireOp",EDGE,"E186");var subQ1=sQuery(id+"F22.wireOp",EDGE,"E195");var subQ2=makeQuery(id+"F22.imprint","INTERSECT",VERTEX,{"derivedFrom":[subQ1,subQ0]});Q8=makeQuery(id+"F22.imprint","IMPRINT",FACE,{"disambiguationData":[TD([[makeQuery(id+"F22.imprint","IMPRINT",EDGE,{"disambiguationData":[TD([[subQ2,1.0]])],"derivedFrom":subQ1}),1.0]])]});}
            var Q9;
            {var subQ0=sQuery(id+"F22.wireOp",EDGE,"E196");var subQ1=sQuery(id+"F22.wireOp",EDGE,"E195");var subQ2=makeQuery(id+"F22.imprint","INTERSECT",VERTEX,{"derivedFrom":[subQ1,subQ0]});Q9=makeQuery(id+"F22.imprint","IMPRINT",FACE,{"disambiguationData":[TD([[makeQuery(id+"F22.imprint","IMPRINT",EDGE,{"disambiguationData":[TD([[subQ2,-1.0]])],"derivedFrom":subQ1}),1.0]])]});}
            var Q10;
            {var subQ0=sQuery(id+"F22.wireOp",EDGE,"E196");var subQ1=sQuery(id+"F22.wireOp",EDGE,"E194");var subQ2=makeQuery(id+"F22.imprint","INTERSECT",VERTEX,{"derivedFrom":[subQ1,subQ0]});Q10=makeQuery(id+"F22.imprint","IMPRINT",FACE,{"disambiguationData":[TD([[makeQuery(id+"F22.imprint","IMPRINT",EDGE,{"disambiguationData":[TD([[subQ2,-1.0]])],"derivedFrom":subQ1}),-1.0]])]});}
            var Q11;
            {var subQ0=sQuery(id+"F22.wireOp",EDGE,"E200");var subQ1=makeQuery(id+"F22.imprint","IMPRINT",VERTEX,{"disambiguationData":[OD(0.0)],"derivedFrom":subQ0});Q11=makeQuery(id+"F22.imprint","IMPRINT",FACE,{"disambiguationData":[TD([[makeQuery(id+"F22.imprint","IMPRINT",EDGE,{"disambiguationData":[TD([[subQ1,-1.0]])],"derivedFrom":subQ0}),-1.0]])]});}
            var Q12;
            {var subQ0=sQuery(id+"F22.wireOp",EDGE,"E200");var subQ1=makeQuery(id+"F22.imprint","IMPRINT",VERTEX,{"disambiguationData":[OD(0.0)],"derivedFrom":subQ0});Q12=makeQuery(id+"F22.imprint","IMPRINT",FACE,{"disambiguationData":[TD([[makeQuery(id+"F22.imprint","IMPRINT",EDGE,{"disambiguationData":[TD([[subQ1,-1.0]])],"derivedFrom":subQ0}),1.0]])]});}
            extrude(context, id + "F23", {"entities" : qUnion([Q0, Q1, Q2, Q3, Q4, Q5, Q6, Q7, Q8, Q9, Q10, Q11, Q12]), "depth" : 3 * mm});
        }
        {
            var Q0;
            Q0=qCreatedBy(makeId("Front.planeOp"),FACE);
            var sketch = newSketch(context, id + "F24", { "sketchPlane" : qUnion([Q0])});
            skLineSegment(sketch, "E210.bottom", {"start": v(-82.37, 66.13) * mm, "end": v(-47.37, 66.13) * mm});
            skLineSegment(sketch, "E210.top", {"start": v(-82.37, 51.13) * mm, "end": v(-47.37, 51.13) * mm});
            skLineSegment(sketch, "E210.left", {"start": v(-82.37, 66.13) * mm, "end": v(-82.37, 51.13) * mm});
            skLineSegment(sketch, "E210.right", {"start": v(-47.37, 66.13) * mm, "end": v(-47.37, 51.13) * mm});
            skLineSegment(sketch, "E211.bottom", {"start": v(-82.37, 66.13) * mm, "end": v(-76.37, 66.13) * mm});
            skLineSegment(sketch, "E211.top", {"start": v(-82.37, 51.13) * mm, "end": v(-76.37, 51.13) * mm});
            skLineSegment(sketch, "E211.right", {"start": v(-76.37, 66.13) * mm, "end": v(-76.37, 51.13) * mm});
            skLineSegment(sketch, "E212.bottom", {"start": v(-47.37, 66.13) * mm, "end": v(-53.37, 66.13) * mm});
            skLineSegment(sketch, "E212.top", {"start": v(-47.37, 51.13) * mm, "end": v(-53.37, 51.13) * mm});
            skLineSegment(sketch, "E212.right", {"start": v(-53.37, 66.13) * mm, "end": v(-53.37, 51.13) * mm});
            skLineSegment(sketch, "E213.top", {"start": v(-82.37, 63.13) * mm, "end": v(-47.37, 63.13) * mm});
            skLineSegment(sketch, "E213.left", {"start": v(-82.37, 66.13) * mm, "end": v(-82.37, 63.13) * mm});
            skLineSegment(sketch, "E213.right", {"start": v(-47.37, 66.13) * mm, "end": v(-47.37, 63.13) * mm});
            skLineSegment(sketch, "E214", {"start": v(-82.37, 66.13) * mm, "end": v(-82.37, 59.13) * mm});
            skLineSegment(sketch, "E215", {"start": v(-82.37, 59.13) * mm, "end": v(-82.37, 56.13) * mm});
            skLineSegment(sketch, "E216", {"start": v(-82.37, 56.13) * mm, "end": v(-82.37, 51.13) * mm});
            skLineSegment(sketch, "E217", {"start": v(-82.37, 56.13) * mm, "end": v(-80.37, 56.13) * mm});
            skLineSegment(sketch, "E218", {"start": v(-80.37, 56.13) * mm, "end": v(-77.37, 56.13) * mm});
            skLineSegment(sketch, "E219", {"start": v(-77.37, 56.13) * mm, "end": v(-76.37, 56.13) * mm});
            skLineSegment(sketch, "E220", {"start": v(-77.37, 56.13) * mm, "end": v(-78.87, 56.13) * mm});
            skLineSegment(sketch, "E221", {"start": v(-78.87, 56.13) * mm, "end": v(-78.87, 57.63) * mm});
            skLineSegment(sketch, "E222", {"start": v(-78.87, 57.63) * mm, "end": v(-47.37, 57.63) * mm});
            skLineSegment(sketch, "E223", {"start": v(-47.37, 57.63) * mm, "end": v(-47.37, 56.13) * mm});
            skLineSegment(sketch, "E224", {"start": v(-47.37, 56.13) * mm, "end": v(-76.37, 56.13) * mm});
            skLineSegment(sketch, "E225", {"start": v(-53.37, 56.13) * mm, "end": v(-50.87, 56.13) * mm});
            skLineSegment(sketch, "E226", {"start": v(-50.87, 56.13) * mm, "end": v(-50.87, 57.63) * mm});
            skCircle(sketch, "E227", {"center": v(-50.87, 57.63) * mm, "radius": 1 * mm});
            skCircle(sketch, "E228", {"center": v(-78.87, 57.63) * mm, "radius": 1 * mm});
            skSolve(sketch);
        }
        {
            var Q0;
            {var subQ0=sQuery(id+"F24.wireOp",EDGE,"E211.top");Q0=makeQuery(id+"F24.imprint","IMPRINT",FACE,{"disambiguationData":[TD([[makeQuery(id+"F24.imprint","IMPRINT",EDGE,{"derivedFrom":subQ0}),1.0]])]});}
            var Q1;
            {var subQ4=sQuery(id+"F24.wireOp",EDGE,"E219");Q1=makeQuery(id+"F24.imprint","IMPRINT",FACE,{"disambiguationData":[TD([[makeQuery(id+"F24.imprint","IMPRINT",EDGE,{"derivedFrom":subQ4}),1.0]])]});}
            var Q2;
            {var subQ0=sQuery(id+"F24.wireOp",EDGE,"E215");Q2=makeQuery(id+"F24.imprint","IMPRINT",FACE,{"disambiguationData":[TD([[makeQuery(id+"F24.imprint","IMPRINT",EDGE,{"derivedFrom":subQ0}),1.0]])]});}
            var Q3;
            {var subQ0=sQuery(id+"F24.wireOp",EDGE,"E210.bottom");var subQ1=sQuery(id+"F24.wireOp",EDGE,"E211.right");var subQ2=makeQuery(id+"F24.imprint","INTERSECT",VERTEX,{"derivedFrom":[subQ1,subQ0]});Q3=makeQuery(id+"F24.imprint","IMPRINT",FACE,{"disambiguationData":[TD([[makeQuery(id+"F24.imprint","IMPRINT",EDGE,{"disambiguationData":[TD([[subQ2,-1.0]])],"derivedFrom":subQ1}),-1.0]])]});}
            var Q4;
            {var subQ0=sQuery(id+"F24.wireOp",EDGE,"E210.bottom");var subQ1=sQuery(id+"F24.wireOp",EDGE,"E211.right");var subQ2=makeQuery(id+"F24.imprint","INTERSECT",VERTEX,{"derivedFrom":[subQ1,subQ0]});Q4=makeQuery(id+"F24.imprint","IMPRINT",FACE,{"disambiguationData":[TD([[makeQuery(id+"F24.imprint","IMPRINT",EDGE,{"disambiguationData":[TD([[subQ2,-1.0]])],"derivedFrom":subQ1}),1.0]])]});}
            var Q5;
            {var subQ5=sQuery(id+"F24.wireOp",EDGE,"E213.right");Q5=makeQuery(id+"F24.imprint","IMPRINT",FACE,{"disambiguationData":[TD([[makeQuery(id+"F24.imprint","IMPRINT",EDGE,{"derivedFrom":subQ5}),-1.0]])]});}
            var Q6;
            {var subQ1=sQuery(id+"F24.wireOp",EDGE,"E212.right");var subQ5=sQuery(id+"F24.wireOp",EDGE,"E213.top");var subQ8=makeQuery(id+"F24.imprint","INTERSECT",VERTEX,{"derivedFrom":[subQ1,subQ5]});Q6=makeQuery(id+"F24.imprint","IMPRINT",FACE,{"disambiguationData":[TD([[makeQuery(id+"F24.imprint","IMPRINT",EDGE,{"disambiguationData":[TD([[subQ8,-1.0]])],"derivedFrom":subQ1}),1.0]])]});}
            var Q7;
            {var subQ1=sQuery(id+"F24.wireOp",EDGE,"E223");Q7=makeQuery(id+"F24.imprint","IMPRINT",FACE,{"disambiguationData":[TD([[makeQuery(id+"F24.imprint","IMPRINT",EDGE,{"derivedFrom":subQ1}),-1.0]])]});}
            var Q8;
            {var subQ0=sQuery(id+"F24.wireOp",EDGE,"E225");Q8=makeQuery(id+"F24.imprint","IMPRINT",FACE,{"disambiguationData":[TD([[makeQuery(id+"F24.imprint","IMPRINT",EDGE,{"derivedFrom":subQ0}),1.0]])]});}
            var Q9;
            {var subQ1=sQuery(id+"F24.wireOp",EDGE,"E212.top");Q9=makeQuery(id+"F24.imprint","IMPRINT",FACE,{"disambiguationData":[TD([[makeQuery(id+"F24.imprint","IMPRINT",EDGE,{"derivedFrom":subQ1}),-1.0]])]});}
            extrude(context, id + "F25", {"entities" : qUnion([Q0, Q1, Q2, Q3, Q4, Q5, Q6, Q7, Q8, Q9]), "depth" : 3 * mm});
        }
        {
            var Q0;
            Q0=qCreatedBy(makeId("Front.planeOp"),FACE);
            var sketch = newSketch(context, id + "F26", { "sketchPlane" : qUnion([Q0])});
            skCircle(sketch, "E229", {"center": v(28.72, -135.08) * mm, "radius": 7.5 * mm});
            skCircle(sketch, "E230", {"center": v(28.72, -135.08) * mm, "radius": 10.5 * mm});
            skLineSegment(sketch, "E231", {"start": v(22.22, -135.08) * mm, "end": v(22.22, -143.33) * mm});
            skLineSegment(sketch, "E232", {"start": v(22.22, -143.33) * mm, "end": v(35.22, -143.33) * mm});
            skLineSegment(sketch, "E233", {"start": v(35.22, -143.33) * mm, "end": v(35.22, -135.08) * mm});
            skLineSegment(sketch, "E234", {"start": v(22.22, -135.08) * mm, "end": v(28.72, -76.68) * mm});
            skLineSegment(sketch, "E235", {"start": v(35.22, -135.08) * mm, "end": v(28.72, -76.68) * mm});
            skLineSegment(sketch, "E236", {"start": v(34.23, -126.14) * mm, "end": v(33.01, -115.2) * mm});
            skLineSegment(sketch, "E237", {"start": v(33.01, -115.2) * mm, "end": v(24.43, -115.2) * mm});
            skLineSegment(sketch, "E238", {"start": v(24.43, -115.2) * mm, "end": v(23.22, -126.14) * mm});
            skLineSegment(sketch, "E239", {"start": v(23.22, -126.14) * mm, "end": v(24.66, -113.22) * mm});
            skLineSegment(sketch, "E240", {"start": v(24.66, -113.22) * mm, "end": v(25.3, -115.2) * mm});
            skLineSegment(sketch, "E241", {"start": v(33.01, -115.2) * mm, "end": v(36.01, -115.2) * mm});
            skLineSegment(sketch, "E242", {"start": v(39.01, -115.2) * mm, "end": v(42.01, -115.2) * mm});
            skLineSegment(sketch, "E243", {"start": v(42.01, -115.2) * mm, "end": v(42.01, -114.7) * mm});
            skLineSegment(sketch, "E244.bottom", {"start": v(42.01, -115.2) * mm, "end": v(39.01, -115.2) * mm});
            skLineSegment(sketch, "E244.top", {"start": v(42.01, -114.7) * mm, "end": v(39.01, -114.7) * mm});
            skLineSegment(sketch, "E244.right", {"start": v(39.01, -115.2) * mm, "end": v(39.01, -114.7) * mm});
            skLineSegment(sketch, "E245", {"start": v(42.01, -115.2) * mm, "end": v(44.83, -115.2) * mm});
            skLineSegment(sketch, "E246", {"start": v(45.01, -115.02) * mm, "end": v(45.01, -112.2) * mm});
            skPoint(sketch, "E247.visualSharp", {"position": v(45.01, -115.2) * mm});
            skArc(sketch, "E247.filletArc", {"start": v(44.83, -115.2) * mm, "mid": v(44.96, -115.15) * mm, "end": v(45.01, -115.02) * mm});
            skLineSegment(sketch, "E248", {"start": v(45.01, -111.2) * mm, "end": v(45.01, -108.39) * mm});
            skLineSegment(sketch, "E249", {"start": v(44.83, -108.2) * mm, "end": v(42.01, -108.2) * mm});
            skLineSegment(sketch, "E250", {"start": v(42.01, -108.2) * mm, "end": v(39.01, -108.2) * mm});
            skLineSegment(sketch, "E251", {"start": v(39.01, -108.2) * mm, "end": v(36.01, -108.2) * mm});
            skPoint(sketch, "E251.endSnap0", {"position": v(40.51, -108.2) * mm});
            skLineSegment(sketch, "E252.bottom", {"start": v(39.01, -108.2) * mm, "end": v(42.01, -108.2) * mm});
            skLineSegment(sketch, "E252.top", {"start": v(39.01, -108.7) * mm, "end": v(42.01, -108.7) * mm});
            skLineSegment(sketch, "E252.left", {"start": v(39.01, -108.2) * mm, "end": v(39.01, -108.7) * mm});
            skLineSegment(sketch, "E252.right", {"start": v(42.01, -108.2) * mm, "end": v(42.01, -108.7) * mm});
            skPoint(sketch, "E253.visualSharp", {"position": v(45.01, -108.2) * mm});
            skArc(sketch, "E253.filletArc", {"start": v(45.01, -108.39) * mm, "mid": v(44.96, -108.26) * mm, "end": v(44.83, -108.2) * mm});
            skLineSegment(sketch, "E254", {"start": v(36.01, -115.2) * mm, "end": v(39.01, -115.2) * mm});
            skLineSegment(sketch, "E255", {"start": v(45.01, -112.2) * mm, "end": v(33.01, -112.2) * mm});
            skLineSegment(sketch, "E256", {"start": v(33.01, -112.2) * mm, "end": v(33.01, -111.2) * mm});
            skLineSegment(sketch, "E257", {"start": v(33.01, -111.2) * mm, "end": v(45.01, -111.2) * mm});
            skLineSegment(sketch, "E258", {"start": v(36.01, -115.2) * mm, "end": v(36.94, -128.55) * mm});
            skLineSegment(sketch, "E259", {"start": v(36.01, -108.2) * mm, "end": v(29.01, -108.2) * mm});
            skLineSegment(sketch, "E260", {"start": v(29.01, -108.2) * mm, "end": v(28.64, -111.57) * mm});
            skLineSegment(sketch, "E261", {"start": v(28.64, -111.57) * mm, "end": v(28.51, -108.2) * mm});
            skLineSegment(sketch, "E262", {"start": v(28.51, -108.2) * mm, "end": v(23.51, -108.2) * mm});
            skLineSegment(sketch, "E263", {"start": v(23.51, -108.2) * mm, "end": v(20.53, -128.51) * mm});
            skLineSegment(sketch, "E264.bottom", {"start": v(30.67, -110.6) * mm, "end": v(31.17, -110.6) * mm});
            skLineSegment(sketch, "E264.top", {"start": v(30.67, -112.6) * mm, "end": v(31.17, -112.6) * mm});
            skLineSegment(sketch, "E264.left", {"start": v(30.67, -110.6) * mm, "end": v(30.67, -112.6) * mm});
            skLineSegment(sketch, "E264.right", {"start": v(31.17, -110.6) * mm, "end": v(31.17, -112.6) * mm});
            skSolve(sketch);
        }
        {
            var Q0;
            {var subQ0=sQuery(id+"F26.wireOp",EDGE,"E241");Q0=makeQuery(id+"F26.imprint","IMPRINT",FACE,{"disambiguationData":[TD([[makeQuery(id+"F26.imprint","IMPRINT",EDGE,{"derivedFrom":subQ0}),1.0]])]});}
            var Q1;
            {var subQ5=sQuery(id+"F26.wireOp",EDGE,"E240");Q1=makeQuery(id+"F26.imprint","IMPRINT",FACE,{"disambiguationData":[TD([[makeQuery(id+"F26.imprint","IMPRINT",EDGE,{"derivedFrom":subQ5}),1.0]])]});}
            var Q2;
            {var subQ8=sQuery(id+"F26.wireOp",EDGE,"E263");Q2=makeQuery(id+"F26.imprint","IMPRINT",FACE,{"disambiguationData":[TD([[makeQuery(id+"F26.imprint","IMPRINT",EDGE,{"derivedFrom":subQ8}),1.0]])]});}
            var Q3;
            {var subQ0=sQuery(id+"F26.wireOp",EDGE,"E236");Q3=makeQuery(id+"F26.imprint","IMPRINT",FACE,{"disambiguationData":[TD([[makeQuery(id+"F26.imprint","IMPRINT",EDGE,{"derivedFrom":subQ0}),-1.0]])]});}
            var Q4;
            {var subQ4=sQuery(id+"F26.wireOp",EDGE,"E235");var subQ6=sQuery(id+"F26.wireOp",EDGE,"E229");var subQ7=makeQuery(id+"F26.imprint","INTERSECT",VERTEX,{"derivedFrom":[subQ6,subQ4]});Q4=makeQuery(id+"F26.imprint","IMPRINT",FACE,{"disambiguationData":[TD([[makeQuery(id+"F26.imprint","IMPRINT",EDGE,{"disambiguationData":[TD([[subQ7,1.0]])],"derivedFrom":subQ6}),-1.0]])]});}
            var Q5;
            {var subQ4=sQuery(id+"F26.wireOp",EDGE,"E229");var subQ6=sQuery(id+"F26.wireOp",EDGE,"E234");var subQ8=makeQuery(id+"F26.imprint","INTERSECT",VERTEX,{"derivedFrom":[subQ4,subQ6]});Q5=makeQuery(id+"F26.imprint","IMPRINT",FACE,{"disambiguationData":[TD([[makeQuery(id+"F26.imprint","IMPRINT",EDGE,{"disambiguationData":[TD([[subQ8,-1.0]])],"derivedFrom":subQ4}),-1.0]])]});}
            extrude(context, id + "F27", {"entities" : qUnion([Q0, Q1, Q2, Q3, Q4, Q5]), "depth" : 25 * mm});
        }
    });
